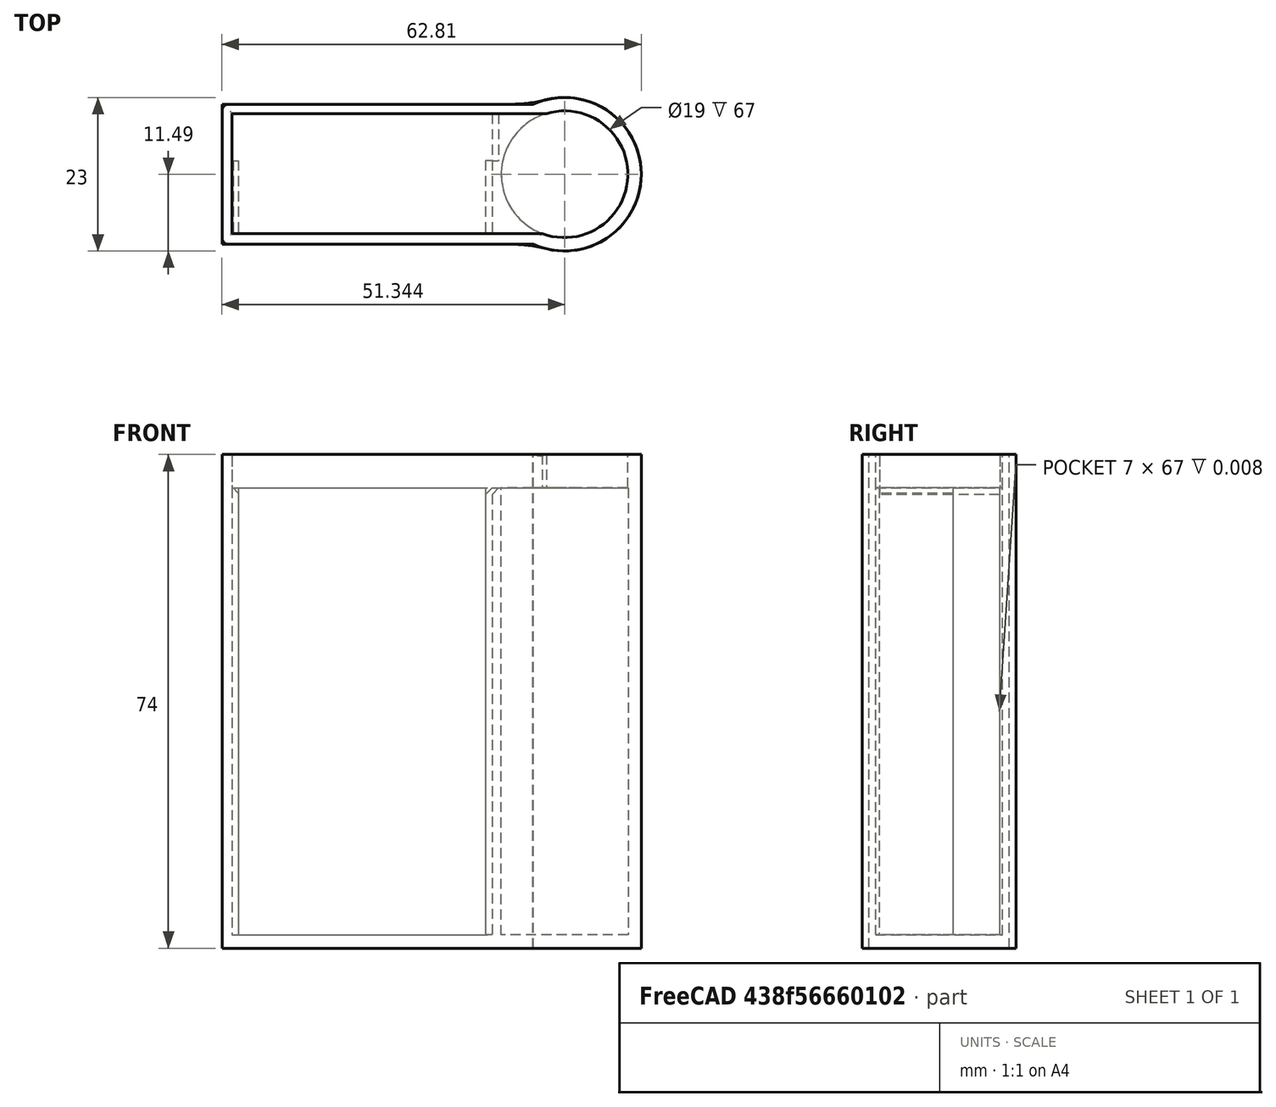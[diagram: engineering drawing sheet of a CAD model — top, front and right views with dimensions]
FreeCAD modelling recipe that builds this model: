
FCSTD DOCUMENT  (FreeCAD 0.16R6706 (Git))
Label: oaps3_gehaeuse
License: All rights reserved
LicenseURL: http://en.wikipedia.org/wiki/All_rights_reserved
objects: PartDesign::Fillet×8, Sketcher::SketchObject×4, PartDesign::Chamfer×3, PartDesign::Pocket×2, PartDesign::Pad×1, Mesh::Feature×1
note: 21 computed .brp shape members not serialized (recipe doc carries the construction recipe); baked Part::Feature solids carry a one-line shape summary decoded from their .brp

FEATURE [Sketcher::SketchObject] Sketch002  label="Grundplatte"
  sketch-geometry (4):
    g0: LineSegment StartX=0.0144881 StartY=21 StartZ=0 EndX=46.6148 EndY=21 EndZ=0
    g1: LineSegment StartX=46.6481 StartY=0 StartZ=0 EndX=0.0144881 EndY=0 EndZ=0
    g2: LineSegment StartX=0.0144881 StartY=0 StartZ=0 EndX=0.0144881 EndY=21 EndZ=0
    g3: ArcOfCircle CenterX=51.3218 CenterY=10.5074 CenterZ=0 NormalX=0 NormalY=0 NormalZ=1 Radius=11.5 StartAngle=4.29387 EndAngle=8.27568
  constraints (11):
    c: Coincident(g1,g2)
    c: Coincident(g2,g0)
    c: Horizontal(g0)
    c: Horizontal(g1)
    c: Vertical(g2)
    c: PointOnObject(g1,g-1)
    c: PointOnObject(g3,g-1)
    c: Radius(g3) = 11.5
    c: Coincident(g3,g0)
    c: Coincident(g3,g1)
    c: Distance(g1,g0) = 21
FEATURE [PartDesign::Pad] Pad
  Length = 74
  Length2 = 100
  Sketch = -> Sketch002
  Type = 0
FEATURE [Sketcher::SketchObject] Sketch  label="Deckelschnitt"
  Placement = pos=(0,0,74) rot=(0,0,1;0rad)
  Support = -> Pad [Face6]
  sketch-geometry (4):
    g0: LineSegment StartX=1.48206 StartY=1.60733 StartZ=0 EndX=47.9995 EndY=1.60733 EndZ=0
    g1: ArcOfCircle CenterX=51.3218 CenterY=10.5074 CenterZ=0 NormalX=0 NormalY=0 NormalZ=1 Radius=9.5 StartAngle=4.35512 EndAngle=8.14524
    g2: LineSegment StartX=1.48206 StartY=19.6073 StartZ=0 EndX=48.5938 EndY=19.6073 EndZ=0
    g3: LineSegment StartX=1.48206 StartY=19.6073 StartZ=0 EndX=1.48206 EndY=1.60733 EndZ=0
  constraints (5):
    c: Radius(g1) = 9.5
    c: Coincident(g1,g0)
    c: Coincident(g2,g1)
    c: Coincident(g3,g0)
    c: Coincident(g3,g2)
FEATURE [PartDesign::Pocket] Pocket
  Length = 5
  Sketch = -> Sketch
  Type = 0
FEATURE [Sketcher::SketchObject] Sketch001  label="Base"
  Placement = pos=(0,0,69) rot=(0,0,1;0rad)
  Support = -> Pocket [Face11]
  sketch-geometry (9):
    g0: Circle CenterX=51.3543 CenterY=10.5 CenterZ=0 NormalX=0 NormalY=0 NormalZ=1 Radius=9.5
    g1: LineSegment StartX=1.47417 StartY=19.5481 StartZ=0 EndX=40.4742 EndY=19.5481 EndZ=0
    g2: LineSegment StartX=1.47417 StartY=19.5481 StartZ=0 EndX=1.47417 EndY=12.5481 EndZ=0
    g3: LineSegment StartX=40.4742 StartY=19.5481 StartZ=0 EndX=40.4742 EndY=12.5481 EndZ=0
    g4: LineSegment StartX=1.47417 StartY=12.5481 StartZ=0 EndX=2.47417 EndY=12.5481 EndZ=0
    g5: LineSegment StartX=2.47417 StartY=12.5481 StartZ=0 EndX=2.47417 EndY=1.5481 EndZ=0
    g6: LineSegment StartX=2.47417 StartY=1.5481 StartZ=0 EndX=39.4742 EndY=1.5481 EndZ=0
    g7: LineSegment StartX=39.4742 StartY=12.5481 StartZ=0 EndX=39.4742 EndY=1.5481 EndZ=0
    g8: LineSegment StartX=40.4742 StartY=12.5481 StartZ=0 EndX=39.4742 EndY=12.5481 EndZ=0
  constraints (19):
    c: Radius(g0) = 9.5
    c: Distance(g1,g1) = 39
    c: Coincident(g3,g1)
    c: Coincident(g2,g1)
    c: Parallel(g2,g3)
    c: Coincident(g4,g2)
    c: Distance(g4,g2) = 1
    c: Angle(g4,g2) = 1.5708
    c: Coincident(g5,g4)
    c: Distance(g5) = 11
    c: Distance(g2) = 7
    c: Coincident(g6,g5)
    c: Coincident(g7,g8)
    c: Equal(g5,g7) = 11
    c: Coincident(g8,g3)
    c: Coincident(g7,g6)
    c: Distance(g8) = 1
    c: Parallel(g7,g5)
    c: Parallel(g8,g1)
FEATURE [Sketcher::SketchObject] Sketch003  label="root"
  Placement = pos=(0,0,69) rot=(0,0,1;0rad)
  Support = -> Pocket [Face11]
  sketch-geometry (13):
    g0: LineSegment StartX=0.013913 StartY=21 StartZ=0 EndX=46.6638 EndY=21 EndZ=0
    g1: LineSegment StartX=46.6638 StartY=0 StartZ=0 EndX=0.013913 EndY=0 EndZ=0
    g2: LineSegment StartX=0.013913 StartY=0 StartZ=0 EndX=0.013913 EndY=21 EndZ=0
    g3: ArcOfCircle CenterX=51.3543 CenterY=10.5 CenterZ=0 NormalX=0 NormalY=0 NormalZ=1 Radius=11.5 StartAngle=4.29228 EndAngle=8.27409
    g4: Circle CenterX=51.3543 CenterY=10.5 CenterZ=0 NormalX=0 NormalY=0 NormalZ=1 Radius=9.5
    g5: LineSegment StartX=1.47417 StartY=19.5481 StartZ=0 EndX=40.4742 EndY=19.5481 EndZ=0
    g6: LineSegment StartX=1.47417 StartY=19.5481 StartZ=0 EndX=1.47417 EndY=12.5481 EndZ=0
    g7: LineSegment StartX=40.4742 StartY=19.5481 StartZ=0 EndX=40.4742 EndY=12.5481 EndZ=0
    g8: LineSegment StartX=1.47417 StartY=12.5481 StartZ=0 EndX=2.47417 EndY=12.5481 EndZ=0
    g9: LineSegment StartX=2.47417 StartY=12.5481 StartZ=0 EndX=2.47417 EndY=1.5481 EndZ=0
    g10: LineSegment StartX=2.47417 StartY=1.5481 StartZ=0 EndX=39.4742 EndY=1.5481 EndZ=0
    g11: LineSegment StartX=39.4742 StartY=12.5481 StartZ=0 EndX=39.4742 EndY=1.5481 EndZ=0
    g12: LineSegment StartX=40.4742 StartY=12.5481 StartZ=0 EndX=39.4742 EndY=12.5481 EndZ=0
  constraints (36):
    c: Coincident(g1,g2)
    c: Coincident(g2,g0)
    c: Horizontal(g0)
    c: Horizontal(g1)
    c: Vertical(g2)
    c: PointOnObject(g1,g-1)
    c: PointOnObject(g3,g-1)
    c: Radius(g3) = 11.5
    c: Coincident(g3,g0)
    c: Coincident(g3,g1)
    c: Distance(g1,g0) = 21
    c: Radius(g4) = 9.5
    c: Coincident(g4,g3)
    c: Distance(g5,g5) = 39
    c: Parallel(g5,g0)
    c: Coincident(g7,g5)
    c: Coincident(g6,g5)
    c: Parallel(g6,g2)
    c: Parallel(g6,g7)
    c: Coincident(g8,g6)
    c: Distance(g8,g6) = 1
    c: Angle(g8,g6) = 1.5708
    c: Coincident(g9,g8)
    c: Parallel(g9,g2)
    c: Distance(g9) = 11
    c: Distance(g6) = 7
    c: Parallel(g10,g1)
    c: Coincident(g10,g9)
    c: Coincident(g11,g12)
    c: Equal(g9,g11) = 11
    c: Coincident(g12,g7)
    c: Coincident(g11,g10)
    c: Distance(g12) = 1
    c: Parallel(g11,g9)
    c: Parallel(g12,g5)
    c: Equal(g0,g1)
FEATURE [PartDesign::Pocket] Pocket001
  Length = 67
  Sketch = -> Sketch001
  Type = 0
FEATURE [PartDesign::Fillet] Fillet
  Base = -> Pocket001 [Edge5]
  Radius = 20
FEATURE [PartDesign::Fillet] Fillet001
  Base = -> Fillet [Edge19]
  Radius = 1
FEATURE [PartDesign::Fillet] Fillet002
  Base = -> Fillet001 [Edge16]
  Radius = 20
FEATURE [PartDesign::Fillet] Fillet003
  Base = -> Fillet002 [Edge15]
  Radius = 1
FEATURE [PartDesign::Fillet] Fillet004
  Base = -> Fillet003 [Edge31]
  Radius = 20
FEATURE [PartDesign::Chamfer] Chamfer
  Base = -> Fillet004 [Edge48]
  Size = 1
FEATURE [PartDesign::Chamfer] Chamfer001
  Base = -> Chamfer [Edge11]
  Size = 1
FEATURE [PartDesign::Chamfer] Chamfer002
  Base = -> Chamfer001 [Edge63]
  Size = 0.8
FEATURE [PartDesign::Fillet] Fillet005
  Base = -> Chamfer002 [Edge26]
  Radius = 0.3
FEATURE [PartDesign::Fillet] Fillet006
  Base = -> Fillet005 [Edge1]
  Radius = 0.3
FEATURE [PartDesign::Fillet] Fillet007
  Base = -> Fillet006 [Edge17]
  Radius = 0.3
FEATURE [Mesh::Feature] NS_LOGO
  Placement = pos=(-87,2.8,177) rot=(1,0,0;1.5708rad)
